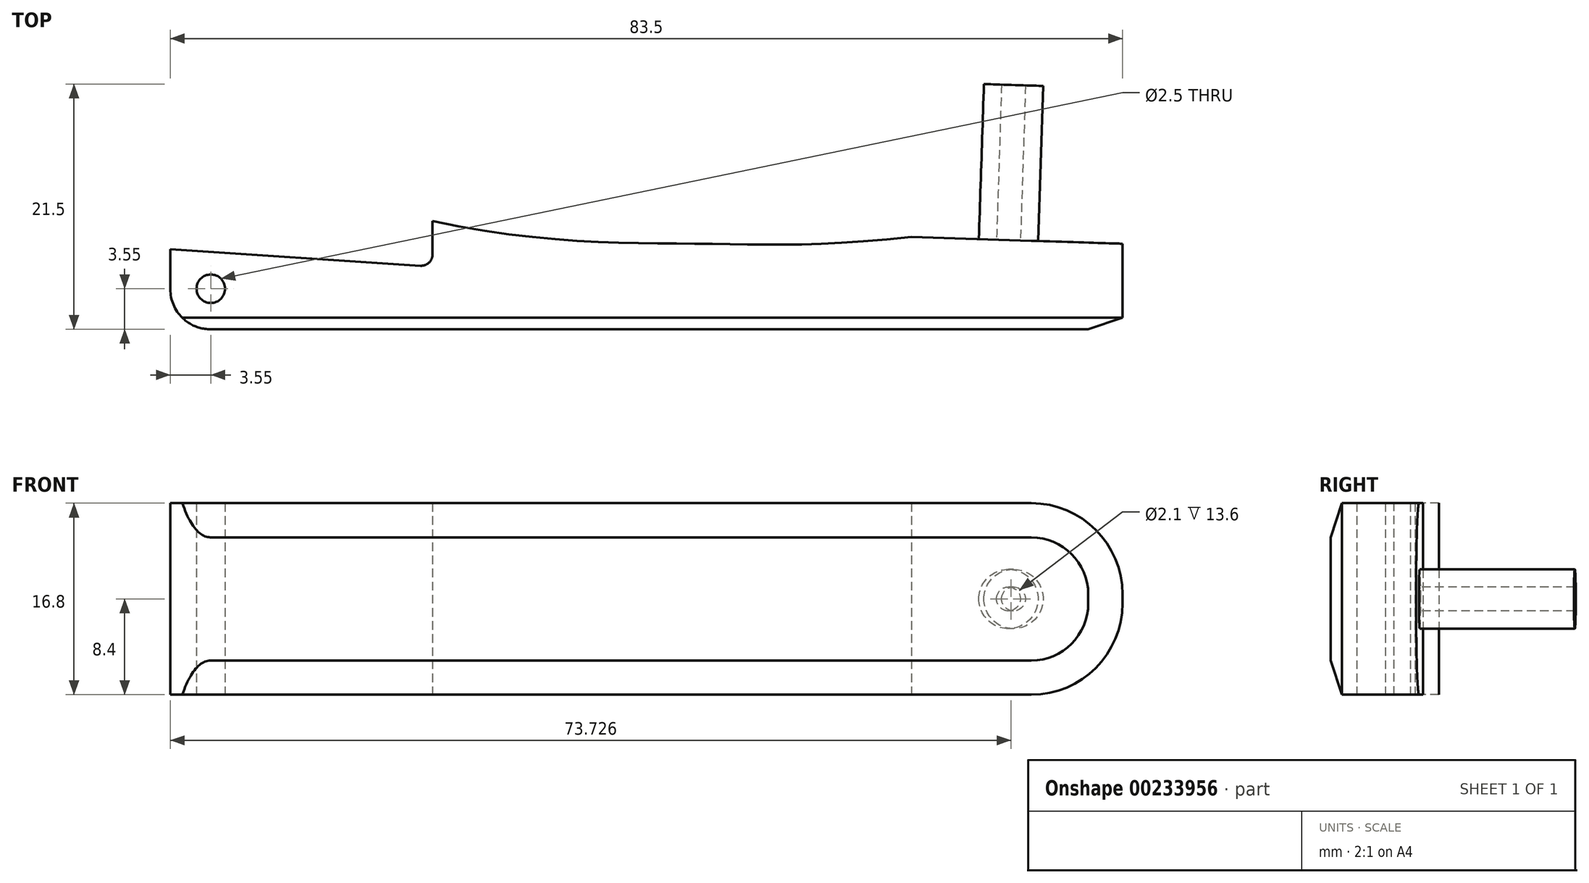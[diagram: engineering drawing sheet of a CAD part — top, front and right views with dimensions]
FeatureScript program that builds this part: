
annotation { "Feature Type Name" : "Feature", "Feature Type Description" : "" }
export const myFeature = defineFeature(function(context is Context, id is Id, definition is map)
    precondition{}
    {
        {
            var Q0;
            Q0=qCreatedBy(makeId("Front.planeOp"),FACE);
            var sketch = newSketch(context, id + "F0", { "sketchPlane" : qUnion([Q0])});
            skLineSegment(sketch, "E0.bottom", {"start": v(41.75, 8.4) * mm, "end": v(-41.75, 8.4) * mm});
            skLineSegment(sketch, "E0.top", {"start": v(41.75, -8.4) * mm, "end": v(-41.75, -8.4) * mm});
            skLineSegment(sketch, "E0.left", {"start": v(41.75, 8.4) * mm, "end": v(41.75, -8.4) * mm});
            skLineSegment(sketch, "E0.right", {"start": v(-41.75, 8.4) * mm, "end": v(-41.75, -8.4) * mm});
            skPoint(sketch, "E0.middle", {"position": v(0, 0) * mm});
            skSolve(sketch);
        }
        {
            var Q0;
            Q0 = qSketchRegion(id + "F0", true);
            var Q1;
            Q1=makeQuery(id+"F0.imprint","IMPRINT",FACE,{"disambiguationData":[TD([[makeQuery(id+"F0.imprint","IMPRINT",EDGE,{"derivedFrom":sQuery(id+"F0.wireOp",EDGE,"E0.bottom")}),1.0]])]});
            extrude(context, id + "F1", {"entities" : qUnion([Q0, Q1]), "depth" : 9.5 * mm});
        }
        {
            var Q0;
            Q0=makeQuery(id+"F1.opExtrude","SWEPT_FACE",FACE,{"disambiguationData":[OSD([sQuery(id+"F0.wireOp",EDGE,"E0.top")])]});
            var sketch = newSketch(context, id + "F2", { "sketchPlane" : qUnion([Q0])});
            skCircle(sketch, "E1", {"center": v(-38.2, 5.95) * mm, "radius": 1.25 * mm});
            skLineSegment(sketch, "E2", {"start": v(-18.75, 9.5) * mm, "end": v(-18.75, 0) * mm});
            skLineSegment(sketch, "E3", {"start": v(-41.75, 2.5) * mm, "end": v(-18.75, 4) * mm});
            skFitSpline(sketch, "E4", {"points": [v(-18.75, 0) * mm, v(4.37, 2) * mm, v(23.25, 1.4) * mm], "startDerivative": vector(54.3, 11.88) * mm, "endDerivative": vector(52, -5.9) * mm});
            skLineSegment(sketch, "E5", {"start": v(23.25, 1.4) * mm, "end": v(41.75, 2) * mm});
            skSolve(sketch);
        }
        {
            var Q0;
            Q0=makeQuery(id+"F2.imprint","IMPRINT",FACE,{"disambiguationData":[TD([[makeQuery(id+"F2.imprint","IMPRINT",EDGE,{"derivedFrom":sQuery(id+"F2.wireOp",EDGE,"E1")}),1.0]])]});
            var Q1;
            {var subQ4=sQuery(id+"F2.wireOp",EDGE,"E3");Q1=makeQuery(id+"F2.imprint","IMPRINT",FACE,{"disambiguationData":[TD([[makeQuery(id+"F2.imprint","IMPRINT",EDGE,{"derivedFrom":subQ4}),-1.0]])]});}
            var Q2;
            {var subQ0=sQuery(id+"F2.wireOp",EDGE,"48992b3b-5875-4d7f-8545-07a0218e9860");Q2=makeQuery(id+"F2.imprint","IMPRINT",FACE,{"disambiguationData":[TD([[makeQuery(id+"F2.imprint","IMPRINT",EDGE,{"derivedFrom":subQ0}),-1.0]])]});}
            var Q3;
            {var subQ0=sQuery(id+"F2.wireOp",EDGE,"E4");Q3=makeQuery(id+"F2.imprint","IMPRINT",FACE,{"disambiguationData":[TD([[makeQuery(id+"F2.imprint","IMPRINT",EDGE,{"derivedFrom":subQ0}),-1.0]])]});}
            extrude(context, id + "F3", {"entities" : qUnion([Q0, Q1, Q2, Q3]), "operationType" : NewBodyOperationType.REMOVE, "oppositeDirection" : true, "depth" : 25 * mm});
        }
        {
            var Q0;
            Q0=makeQuery(id+"F3.boolean.opBoolean","COPY",FACE,{"derivedFrom":makeQuery(id+"F3.opExtrude","SWEPT_FACE",FACE,{"disambiguationData":[OSD([sQuery(id+"F2.wireOp",EDGE,"E5")])]})});
            var sketch = newSketch(context, id + "F4", { "sketchPlane" : qUnion([Q0])});
            skCircle(sketch, "E6", {"center": v(-31.8, 0) * mm, "radius": 2.6 * mm});
            skCircle(sketch, "E7", {"center": v(-31.8, 0) * mm, "radius": 1.05 * mm});
            skSolve(sketch);
        }
        {
            var Q0;
            Q0=makeQuery(id+"F4.imprint","IMPRINT",FACE,{"disambiguationData":[TD([[makeQuery(id+"F4.imprint","IMPRINT",EDGE,{"derivedFrom":sQuery(id+"F4.wireOp",EDGE,"E6")}),1.0]])]});
            extrude(context, id + "F5", {"entities" : qUnion([Q0]), "operationType" : NewBodyOperationType.ADD, "depth" : 13.6 * mm});
        }
        {
            var Q0;
            Q0=makeQuery(id+"F3.boolean.opBoolean","COPY",EDGE,{"derivedFrom":makeQuery(id+"F3.opExtrude","SWEPT_EDGE",EDGE,{"disambiguationData":[OSD([sQuery(id+"F2.wireOp",EDGE,"E2"),sQuery(id+"F2.wireOp",EDGE,"E3")])]})});
            var Q1;
            {var subQ0=sQuery(id+"F2.wireOp",EDGE,"E4");var subQ1=sQuery(id+"F0.wireOp",EDGE,"E0.top");var subQ2=sQuery(id+"F2.wireOp",EDGE,"E2");Q1=makeQuery(id+"F3.boolean.opBoolean","TWEAK_EDGE",EDGE,{"derivedFrom":[makeQuery(id+"F3.opExtrude","SWEPT_EDGE",EDGE,{"disambiguationData":[OSD([subQ1,subQ2,subQ0]),ownerDisambiguation([makeQuery(id+"F3.opExtrude","SWEPT_BODY",BODY,{"disambiguationData":[OSD([subQ1,sQuery(id+"F0.wireOp",EDGE,"E0.right"),subQ2,sQuery(id+"F2.wireOp",EDGE,"E3")])]})])]}),makeQuery(id+"F3.opExtrude","SWEPT_EDGE",EDGE,{"disambiguationData":[OSD([subQ1,subQ2,subQ0]),ownerDisambiguation([makeQuery(id+"F3.opExtrude","SWEPT_BODY",BODY,{"disambiguationData":[OSD([subQ1,sQuery(id+"F0.wireOp",EDGE,"E0.left"),subQ0,sQuery(id+"F2.wireOp",EDGE,"E5")])]})])]})]});}
            var Q2;
            Q2=makeQuery(id+"F5.opExtrude","CAP_EDGE",EDGE,{"disambiguationData":[OSD([sQuery(id+"F4.wireOp",EDGE,"E6")])],"isStart":true});
            fillet(context, id + "F6", {"entities" : qUnion([Q0, Q1, Q2]), "radius" : 1 * mm, "tangentPropagation" : true, "allowEdgeOverflow" : false});
        }
        {
            var Q0;
            Q0=makeQuery(id+"F1.opExtrude","SWEPT_EDGE",EDGE,{"disambiguationData":[OSD([sQuery(id+"F0.wireOp",EDGE,"E0.bottom"),sQuery(id+"F0.wireOp",EDGE,"E0.left")])]});
            var Q1;
            Q1=makeQuery(id+"F1.opExtrude","SWEPT_EDGE",EDGE,{"disambiguationData":[OSD([sQuery(id+"F0.wireOp",EDGE,"E0.top"),sQuery(id+"F0.wireOp",EDGE,"E0.left")])]});
            fillet(context, id + "F7", {"entities" : qUnion([Q0, Q1]), "radius" : 8 * mm, "tangentPropagation" : true, "allowEdgeOverflow" : false});
        }
        {
            var Q0;
            Q0=makeQuery(id+"F1.opExtrude","CAP_EDGE",EDGE,{"disambiguationData":[OSD([sQuery(id+"F0.wireOp",EDGE,"E0.bottom")])],"isStart":false});
            chamfer(context, id + "F8", {"entities" : qUnion([Q0]), "chamferType" : ChamferType.TWO_OFFSETS, "width1" : 3 * mm, "oppositeDirection" : false, "width2" : 1 * mm, "tangentPropagation" : true});
        }
        {
            var Q0;
            Q0=makeQuery(id+"F3.boolean.opBoolean","COPY",EDGE,{"derivedFrom":makeQuery(id+"F3.opExtrude","SWEPT_EDGE",EDGE,{"disambiguationData":[OSD([sQuery(id+"F0.wireOp",EDGE,"E0.top"),sQuery(id+"F0.wireOp",EDGE,"E0.right"),sQuery(id+"F2.wireOp",EDGE,"E3")])]})});
            var Q1;
            Q1=makeQuery(id+"F1.opExtrude","CAP_EDGE",EDGE,{"disambiguationData":[OSD([sQuery(id+"F0.wireOp",EDGE,"E0.right")])],"isStart":false});
            fillet(context, id + "F9", {"entities" : qUnion([Q0, Q1]), "radius" : 3.5 * mm, "tangentPropagation" : true, "allowEdgeOverflow" : false});
        }
    });
